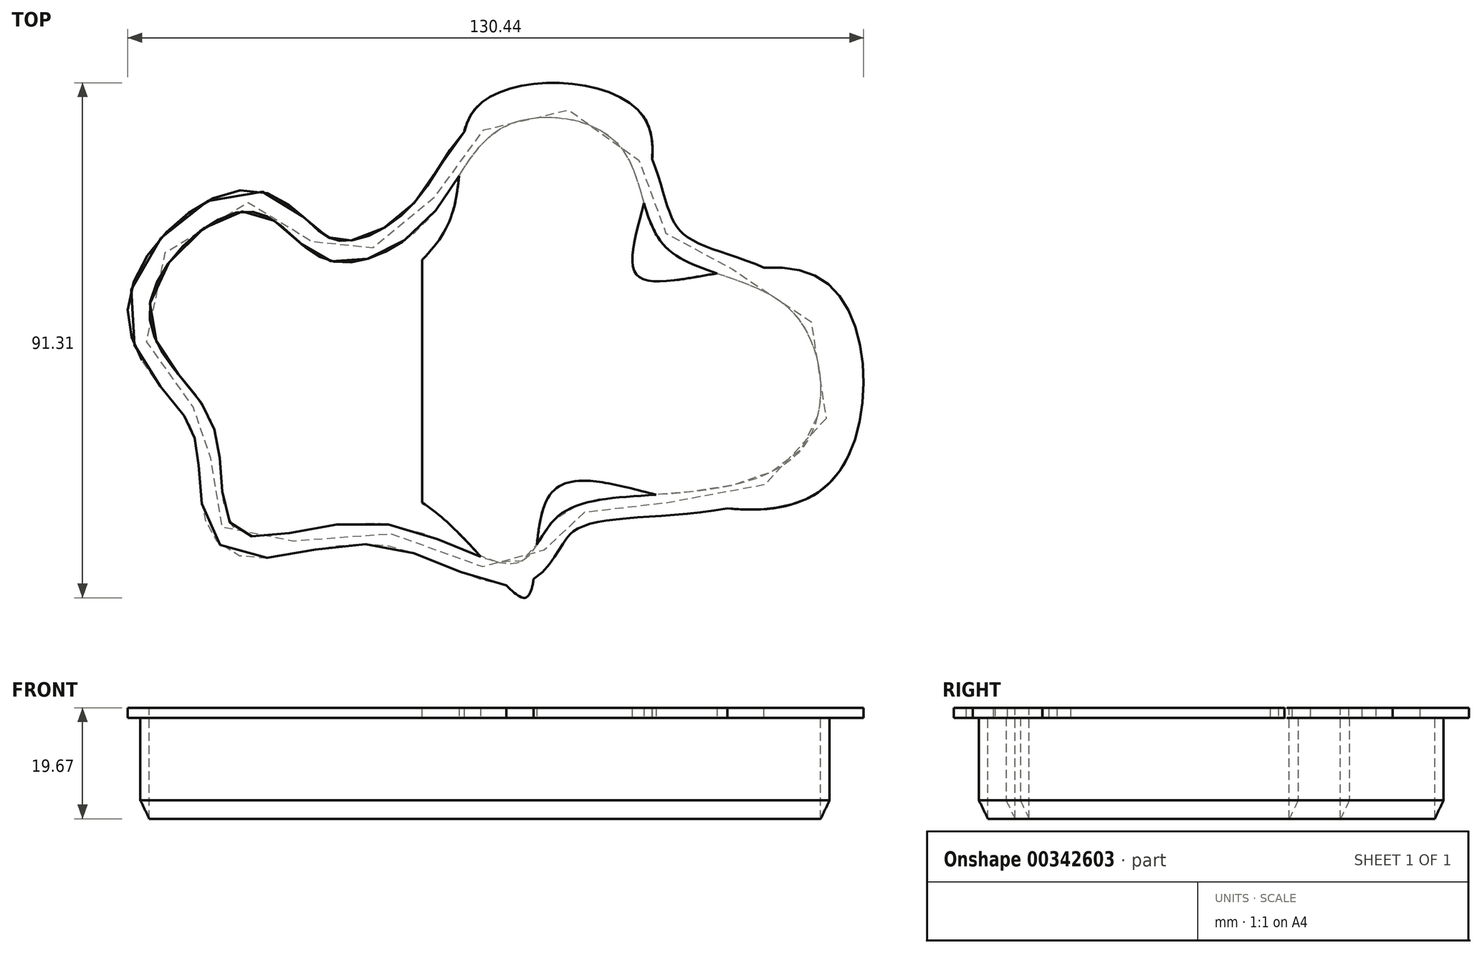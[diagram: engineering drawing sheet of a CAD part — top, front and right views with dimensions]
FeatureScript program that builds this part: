
annotation { "Feature Type Name" : "Feature", "Feature Type Description" : "" }
export const myFeature = defineFeature(function(context is Context, id is Id, definition is map)
    precondition{}
    {
        {
            var Q0;
            Q0=qCreatedBy(makeId("Top.planeOp"),FACE);
            var sketch = newSketch(context, id + "F0", { "sketchPlane" : qUnion([Q0])});
            skFitSpline(sketch, "E0", {"points": [v(-53.76, 0) * mm, v(-62.79, 16.94) * mm, v(-45.18, 33.78) * mm, v(-31.67, 25.26) * mm, v(-13.34, 32.42) * mm, v(0, 48.78) * mm, v(20.27, 45.72) * mm, v(28.58, 27.57) * mm, v(50.66, 16.48) * mm, v(53.6, -7.26) * mm, v(28.86, -16.33) * mm, v(9.35, -20.49) * mm, v(2.38, -28.56) * mm, v(-22.01, -21.53) * mm, v(-46.9, -23.19) * mm, v(-50.27, -11.07) * mm, v(-53.76, 0) * mm]});
            skLineSegment(sketch, "E1", {"start": v(55.6, -2.57) * mm, "end": v(59.3, -3.49) * mm});
            skSolve(sketch);
        }
        {
            var Q0;
            Q0=sQuery(id+"F0.wireOp",EDGE,"E1");
            extrude(context, id + "F1", {"bodyType" : ToolBodyType.SURFACE, "surfaceEntities" : qUnion([Q0]), "oppositeDirection" : true, "depth" : 25 * mm});
        }
        {
            var Q0;
            Q0=makeQuery(id+"F1.opExtrude","SWEPT_FACE",FACE,{"disambiguationData":[OSD([sQuery(id+"F0.wireOp",EDGE,"E1")])]});
            var sketch = newSketch(context, id + "F2", { "sketchPlane" : qUnion([Q0])});
            skLineSegment(sketch, "E2", {"start": v(-58.39, 0) * mm, "end": v(-58.39, -1.78) * mm});
            skLineSegment(sketch, "E3", {"start": v(-58.39, -1.78) * mm, "end": v(-56.16, -1.78) * mm});
            skLineSegment(sketch, "E4", {"start": v(-56.16, -1.78) * mm, "end": v(-56.16, -16.4) * mm});
            skLineSegment(sketch, "E5", {"start": v(-56.16, -16.4) * mm, "end": v(-54.58, -19.67) * mm});
            skLineSegment(sketch, "E6", {"start": v(-54.58, -19.67) * mm, "end": v(-54.58, 0) * mm});
            skLineSegment(sketch, "E7", {"start": v(-54.58, 0) * mm, "end": v(-58.39, 0) * mm});
            skSolve(sketch);
        }
        {
            var Q0;
            Q0=makeQuery(id+"F2.imprint","IMPRINT",FACE,{"disambiguationData":[TD([[makeQuery(id+"F2.imprint","IMPRINT",EDGE,{"derivedFrom":sQuery(id+"F2.wireOp",EDGE,"E2")}),1.0]])]});
            var Q1;
            Q1=sQuery(id+"F0.wireOp",EDGE,"E0");
            sweep(context, id + "F3", {"profiles" : qUnion([Q0]), "path" : qUnion([Q1])});
        }
        {
            var Q0;
            Q0=qCreatedBy(makeId("Top.planeOp"),FACE);
            var sketch = newSketch(context, id + "F4", { "sketchPlane" : qUnion([Q0])});
            skLineSegment(sketch, "E8", {"start": v(-14.5, -23.28) * mm, "end": v(-14.5, 31.22) * mm});
            skLineSegment(sketch, "E9", {"start": v(13.95, -18.06) * mm, "end": v(13.95, -18.06) * mm});
            skFitSpline(sketch, "E10", {"points": [v(-53.76, 0) * mm, v(-57.05, 4.65) * mm, v(-70.88, 16.28) * mm, v(-43.67, 41.63) * mm, v(-33.18, 19.88) * mm, v(-10.23, 30.8) * mm, v(-3.95, 53.07) * mm, v(25.35, 49.55) * mm, v(23.54, 22.55) * mm, v(55.42, 22.27) * mm, v(59.23, -12.68) * mm, v(29.04, -16.97) * mm, v(7.9, -16.88) * mm, v(3.85, -34.7) * mm, v(-21.4, -15.22) * mm, v(-50.03, -29.5) * mm, v(-49.92, -10) * mm, v(-51.2, -3.62) * mm, v(-53.76, 0) * mm]});
            skFitSpline(sketch, "E11", {"points": [v(-53.76, 0) * mm, v(-57.05, 4.65) * mm, v(-70.88, 16.28) * mm, v(-43.67, 41.63) * mm, v(-33.18, 19.88) * mm, v(-10.23, 30.8) * mm, v(-3.95, 53.07) * mm, v(25.35, 49.55) * mm, v(23.54, 22.55) * mm, v(55.42, 22.27) * mm, v(59.23, -12.68) * mm, v(29.04, -16.97) * mm, v(7.9, -16.88) * mm, v(3.85, -34.7) * mm, v(-21.4, -15.22) * mm, v(-50.03, -29.5) * mm, v(-49.92, -10) * mm, v(-51.2, -3.62) * mm, v(-53.76, 0) * mm]});
            skLineSegment(sketch, "E12", {"start": v(13.95, -18.06) * mm, "end": v(13.95, 49.54) * mm});
            skFitSpline(sketch, "E13", {"points": [v(-53.76, 0) * mm, v(-57.05, 4.65) * mm, v(-70.88, 16.28) * mm, v(-43.67, 41.63) * mm, v(-33.18, 19.88) * mm, v(-10.23, 30.8) * mm, v(-3.95, 53.07) * mm, v(25.35, 49.55) * mm, v(23.54, 22.55) * mm, v(55.42, 22.27) * mm, v(59.23, -12.68) * mm, v(29.04, -16.97) * mm, v(7.9, -16.88) * mm, v(3.85, -34.7) * mm, v(-21.4, -15.22) * mm, v(-50.03, -29.5) * mm, v(-49.92, -10) * mm, v(-51.2, -3.62) * mm, v(-53.76, 0) * mm]});
            skSolve(sketch);
        }
        {
            var Q0;
            {var subQ0=sQuery(id+"F4.wireOp",EDGE,"E8");Q0=makeQuery(id+"F4.imprint","IMPRINT",FACE,{"disambiguationData":[TD([[makeQuery(id+"F4.imprint","IMPRINT",EDGE,{"derivedFrom":subQ0}),-1.0]])]});}
            var Q1;
            Q1=makeQuery(id+"F3.opSweep","SWEPT_FACE",FACE,{"disambiguationData":[OSD([sQuery(id+"F0.wireOp",EDGE,"E0"),sQuery(id+"F2.wireOp",EDGE,"E3")])]});
            extrude(context, id + "F5", {"entities" : qUnion([Q0]), "operationType" : NewBodyOperationType.ADD, "endBound" : BoundingType.UP_TO_SURFACE, "oppositeDirection" : true, "endBoundEntityFace" : qUnion([Q1]), "depth" : 25 * mm});
        }
    });
